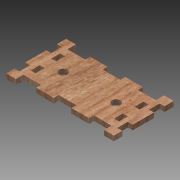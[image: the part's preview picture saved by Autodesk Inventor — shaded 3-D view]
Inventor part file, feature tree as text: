
AUTODESK INVENTOR PART (.ipt)
format: ipt  version: 2014 SP1 (Build 180222100, 222)  size: 371,200 bytes
history: native  units: mm
features: other x10, sketch x9, extrude x5, hole x1
ambient origin geometry x8: Origin, YZ Plane, XZ Plane, XY Plane, X Axis, Y Axis, Z Axis, Center Point
bodies: Body1 (feature_tree)
feature tree (25):
  other  "Blocks"
  extrude  "Extrusion2"  Depth=50.0mm
  hole  "Hole5"  [1 undecoded]
  extrude  "Extrusion6"  Depth=20.0mm
  extrude  "Extrusion7"  Depth=5.5mm
  extrude  "Extrusion8"  TaperAngle=0.0deg  [1 undecoded]
  extrude  "Extrusion10"  Depth=10.0mm
  sketch  "Sketch46"  dims[d147=5.5mm]
  sketch  "Sketch47"  dims[d148=0.0mm d155=11.0mm d162=5.5mm d163=0.0mm d164=5.5mm d165=12.0mm d166=12.0mm d172=5.5mm d173=0.0mm d29=1.0mm d30=1.0mm d116=1.0mm d117=1.0mm]
  sketch  "Sketch44"  dims[d146=8.333333mm]
  other  "Kerf0.1"
  sketch  "Sketch10"  dims[d21=100.0mm d22=50.0mm]
  sketch  "Sketch16"  dims[d23=5.5mm d24=0.0mm d52=60.0mm]
  sketch  "Sketch35"  dims[d53=9.5mm d54=6.0mm d55=4.0mm d56=2.0mm d57=90.0deg d58=4.0mm d59=0.0mm d129=20.0mm]
  sketch  "Sketch36"  dims[d130=20.0mm d131=5.5mm]
  sketch  "Sketch37"  dims[d142=5.5mm d143=0.0mm]
  sketch  "Sketch38"  dims[d144=5.5mm d145=10.0mm]
  other  "Block1"
  other  "Block2"
  other  "Block3"
  other  "Block4"
  other  "Block3:1"
  other  "Block3:2"
  other  "Block4:1"
  other  "Block4:2"
note: 2 required parameter values undecoded (feature->parameter linkage not recoverable at this tier; creation-order binding heuristic only, values carry confidence <= 0.55)
